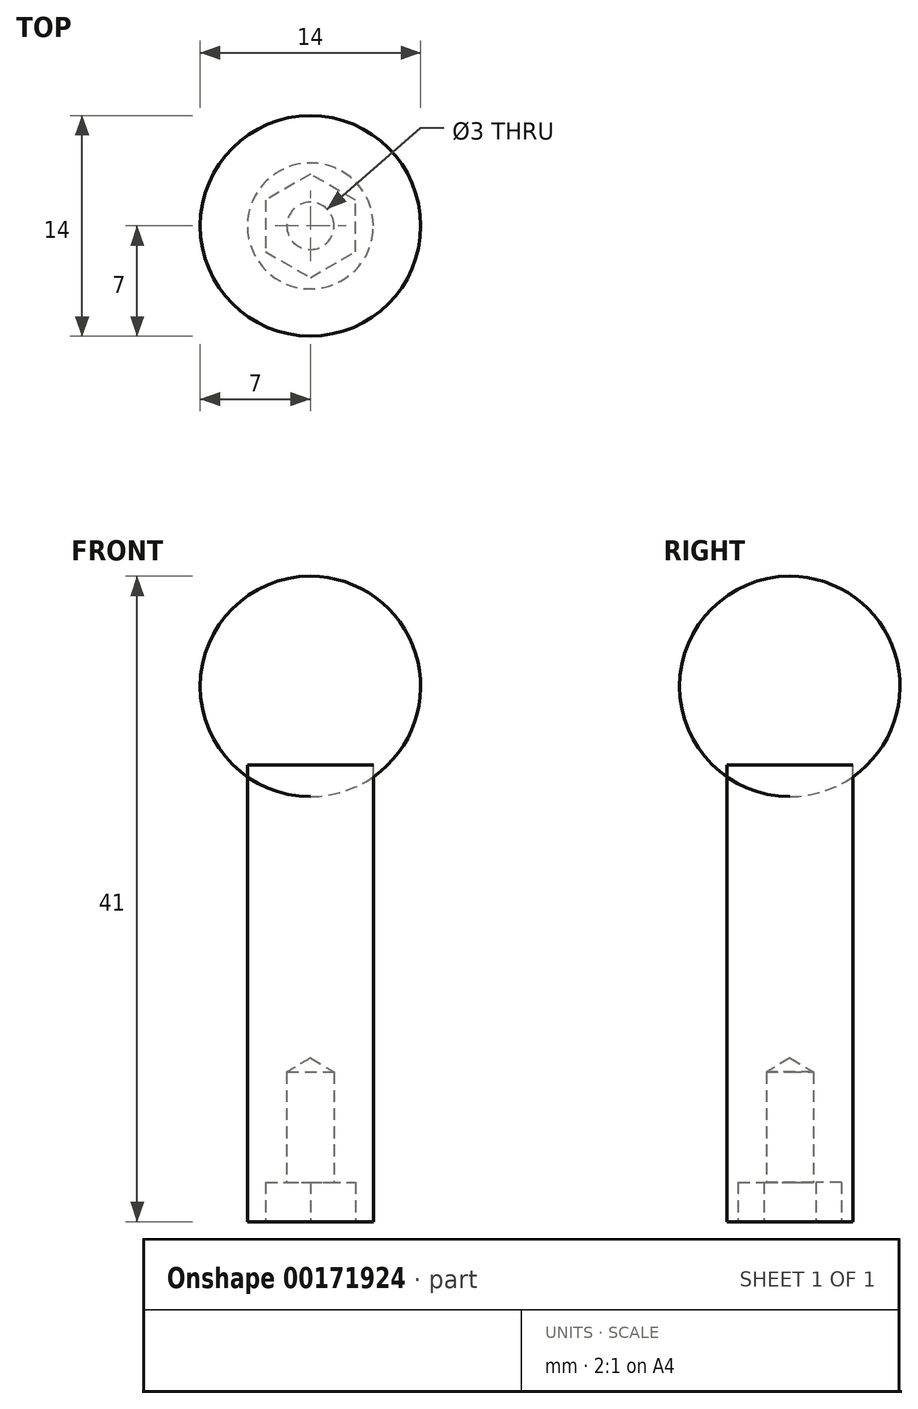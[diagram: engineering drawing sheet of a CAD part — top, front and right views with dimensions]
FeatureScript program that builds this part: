
annotation { "Feature Type Name" : "Feature", "Feature Type Description" : "" }
export const myFeature = defineFeature(function(context is Context, id is Id, definition is map)
    precondition{}
    {
        {
            var Q0;
            Q0=qCreatedBy(makeId("Top.planeOp"),FACE);
            var sketch = newSketch(context, id + "F0", { "sketchPlane" : qUnion([Q0])});
            skPoint(sketch, "E0.0.midPoint", {"position": v(3.46, 0) * mm});
            skCircle(sketch, "E1", {"center": v(0, 0) * mm, "radius": 4 * mm});
            skPoint(sketch, "E2.orphan", {"position": v(-3.46, -2) * mm});
            skPoint(sketch, "E3.orphan", {"position": v(3.46, 2) * mm});
            skPoint(sketch, "E0.1.start.orphan", {"position": v(3.46, -2) * mm});
            skSolve(sketch);
        }
        {
            var Q0;
            Q0 = qSketchRegion(id + "F0", true);
            extrude(context, id + "F1", {"entities" : qUnion([Q0]), "endBound" : BoundingType.SYMMETRIC, "oppositeDirection" : true, "depth" : 4 * mm});
        }
        {
            var Q0;
            Q0=qCreatedBy(makeId("Right.planeOp"),FACE);
            var sketch = newSketch(context, id + "F2", { "sketchPlane" : qUnion([Q0])});
            skArc(sketch, "E4", {"start": v(0, 14) * mm, "mid": v(-7, 7) * mm, "end": v(0, 0) * mm});
            skPoint(sketch, "E5.orphan", {"position": v(0, 15.06) * mm});
            skLineSegment(sketch, "E6", {"start": v(0, 15.54) * mm, "end": v(0, -0.97) * mm});
            skSolve(sketch);
        }
        {
            var Q0;
            {var subQ0=sQuery(id+"F2.wireOp",EDGE,"E4");Q0=makeQuery(id+"F2.imprint","IMPRINT",FACE,{"disambiguationData":[TD([[makeQuery(id+"F2.imprint","IMPRINT",EDGE,{"derivedFrom":subQ0}),1.0]])]});}
            var Q1;
            Q1=sQuery(id+"F2.wireOp",EDGE,"E6");
            revolve(context, id + "F3", {"entities" : qUnion([Q0]), "axis" : qUnion([Q1]), "revolveType" : RevolveType.FULL});
        }
        {
            var Q0;
            Q0=makeQuery(id+"F1.opExtrude","CAP_FACE",FACE,{"disambiguationData":[OSD([sQuery(id+"F0.wireOp",EDGE,"E1")])],"isStart":false});
            extrude(context, id + "F4", {"entities" : qUnion([Q0]), "operationType" : NewBodyOperationType.ADD, "depth" : 25 * mm});
        }
        {
            var Q0;
            Q0=makeQuery(id+"F4.opExtrude","CAP_FACE",FACE,{"disambiguationData":[OSD([sQuery(id+"F0.wireOp",EDGE,"E1")])],"isStart":false});
            var sketch = newSketch(context, id + "F5", { "sketchPlane" : qUnion([Q0])});
            skCircle(sketch, "E7", {"center": v(0, 0) * mm, "radius": 1.5 * mm});
            skSolve(sketch);
        }
        {
            var Q0;
            Q0=sQuery(id+"F5.wireOp",VERTEX,"E7.center");
            var Q1;
            Q1=makeQuery(id+"F1.opExtrude","SWEPT_BODY",BODY,{"disambiguationData":[OSD([sQuery(id+"F0.wireOp",EDGE,"E1")])]});
            hole(context, id + "F6", {"style" : HoleStyle.C_BORE, "endStyle" : HoleEndStyle.BLIND, "holeDiameter" : 3 * mm, "cBoreDiameter" : 3 * mm, "cBoreDepth" : 9.5 * mm, "holeDepth" : 9.5 * mm, "isTappedThrough" : true, "tappedDepth" : 12 * mm, "tapClearance" : 3, "locations" : qUnion([Q0]), "scope" : qUnion([Q1])});
        }
        {
            var Q0;
            Q0=makeQuery(id+"F4.opExtrude","CAP_FACE",FACE,{"disambiguationData":[OSD([sQuery(id+"F0.wireOp",EDGE,"E1")])],"isStart":false});
            var sketch = newSketch(context, id + "F7", { "sketchPlane" : qUnion([Q0])});
            skCircle(sketch, "E8.cCircle", {"center": v(0, 0) * mm, "radius": 2.85 * mm, "construction": true});
            skLineSegment(sketch, "E8.0", {"start": v(2.85, 1.65) * mm, "end": v(2.85, -1.65) * mm});
            skLineSegment(sketch, "E8.1", {"start": v(2.85, -1.65) * mm, "end": v(0, -3.3) * mm});
            skLineSegment(sketch, "E8.2", {"start": v(0, -3.3) * mm, "end": v(-2.85, -1.65) * mm});
            skLineSegment(sketch, "E8.3", {"start": v(-2.85, -1.65) * mm, "end": v(-2.85, 1.65) * mm});
            skLineSegment(sketch, "E8.4", {"start": v(-2.85, 1.65) * mm, "end": v(0, 3.3) * mm});
            skLineSegment(sketch, "E8.5", {"start": v(0, 3.3) * mm, "end": v(2.85, 1.65) * mm});
            skPoint(sketch, "E8.0.midPoint", {"position": v(2.85, 0) * mm});
            skSolve(sketch);
        }
        {
            var Q0;
            Q0 = qSketchRegion(id + "F7", true);
            extrude(context, id + "F8", {"entities" : qUnion([Q0]), "operationType" : NewBodyOperationType.REMOVE, "oppositeDirection" : true, "depth" : 2.5 * mm});
        }
    });
